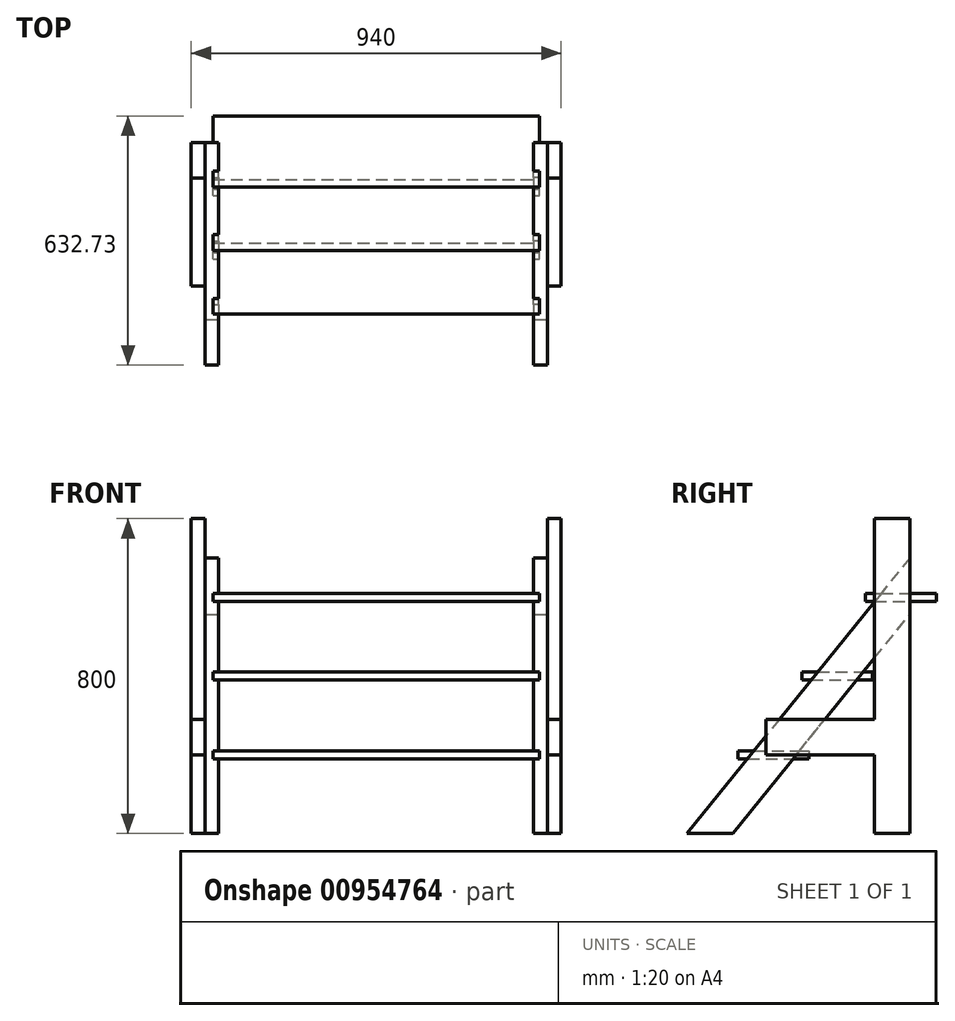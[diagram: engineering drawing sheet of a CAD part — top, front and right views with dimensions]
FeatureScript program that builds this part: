
annotation { "Feature Type Name" : "Feature", "Feature Type Description" : "" }
export const myFeature = defineFeature(function(context is Context, id is Id, definition is map)
    precondition{}
    {
        {
            var Q0;
            Q0=qCreatedBy(makeId("Right.planeOp"),FACE);
            var sketch = newSketch(context, id + "F0", { "sketchPlane" : qUnion([Q0])});
            skLineSegment(sketch, "E0.bottom", {"start": v(316.77, -269.2) * mm, "end": v(226.77, -269.2) * mm});
            skLineSegment(sketch, "E0.top", {"start": v(316.77, 530.8) * mm, "end": v(226.77, 530.8) * mm});
            skLineSegment(sketch, "E0.left", {"start": v(316.77, -269.2) * mm, "end": v(316.77, 530.8) * mm});
            skLineSegment(sketch, "E0.right", {"start": v(226.77, -269.2) * mm, "end": v(226.77, 530.8) * mm});
            skSolve(sketch);
        }
        {
            var Q0;
            Q0=makeQuery(id+"F0.imprint","IMPRINT",FACE,{"disambiguationData":[TD([[makeQuery(id+"F0.imprint","IMPRINT",EDGE,{"derivedFrom":sQuery(id+"F0.wireOp",EDGE,"E0.bottom")}),-1.0]])]});
            extrude(context, id + "F1", {"entities" : qUnion([Q0]), "depth" : 35 * mm, "offsetDistance" : 25 * mm});
        }
        {
            var Q0;
            Q0=makeQuery(id+"F1.opExtrude","CAP_FACE",FACE,{"disambiguationData":[OSD([sQuery(id+"F0.wireOp",EDGE,"E0.bottom"),sQuery(id+"F0.wireOp",EDGE,"E0.top"),sQuery(id+"F0.wireOp",EDGE,"E0.left"),sQuery(id+"F0.wireOp",EDGE,"E0.right")])],"isStart":true});
            var sketch = newSketch(context, id + "F2", { "sketchPlane" : qUnion([Q0])});
            skLineSegment(sketch, "E1", {"start": v(-316.77, 430.8) * mm, "end": v(248.91, -269.2) * mm});
            skLineSegment(sketch, "E2", {"start": v(-84.35, 0) * mm, "end": v(-316.77, 287.6) * mm});
            skLineSegment(sketch, "E3", {"start": v(-84.35, 0) * mm, "end": v(133.2, -269.2) * mm});
            skLineSegment(sketch, "E4", {"start": v(-316.77, 430.8) * mm, "end": v(-316.77, 287.6) * mm});
            skLineSegment(sketch, "E5", {"start": v(248.91, -269.2) * mm, "end": v(133.2, -269.2) * mm});
            skSolve(sketch);
        }
        {
            var Q0;
            Q0 = qSketchRegion(id + "F2", true);
            extrude(context, id + "F3", {"entities" : qUnion([Q0]), "operationType" : NewBodyOperationType.ADD, "depth" : 35 * mm, "offsetDistance" : 25 * mm});
        }
        {
            var Q0;
            Q0=makeQuery(id+"F1.opExtrude","SWEPT_FACE",FACE,{"disambiguationData":[OSD([sQuery(id+"F0.wireOp",EDGE,"E0.right")])]});
            var sketch = newSketch(context, id + "F4", { "sketchPlane" : qUnion([Q0])});
            skLineSegment(sketch, "E6", {"start": v(35, -69.2) * mm, "end": v(35, 23.34) * mm});
            skLineSegment(sketch, "E7.bottom", {"start": v(35, -69.2) * mm, "end": v(0, -69.2) * mm});
            skLineSegment(sketch, "E7.top", {"start": v(35, 20.8) * mm, "end": v(0, 20.8) * mm});
            skLineSegment(sketch, "E7.left", {"start": v(35, -69.2) * mm, "end": v(35, 20.8) * mm});
            skLineSegment(sketch, "E7.right", {"start": v(0, -69.2) * mm, "end": v(0, 20.8) * mm});
            skSolve(sketch);
        }
        {
            var Q0;
            Q0=makeQuery(id+"F3.opExtrude","CAP_FACE",FACE,{"disambiguationData":[OSD([sQuery(id+"F2.wireOp",EDGE,"E1"),sQuery(id+"F2.wireOp",EDGE,"E2"),sQuery(id+"F2.wireOp",EDGE,"E3"),sQuery(id+"F2.wireOp",EDGE,"E4"),sQuery(id+"F2.wireOp",EDGE,"E5")])],"isStart":false});
            var sketch = newSketch(context, id + "F5", { "sketchPlane" : qUnion([Q0])});
            skLineSegment(sketch, "E8.bottom", {"start": v(119.43, -59.2) * mm, "end": v(-60.57, -59.2) * mm});
            skLineSegment(sketch, "E8.top", {"start": v(119.43, -79.2) * mm, "end": v(-60.57, -79.2) * mm});
            skLineSegment(sketch, "E8.left", {"start": v(119.43, -59.2) * mm, "end": v(119.43, -79.2) * mm});
            skLineSegment(sketch, "E8.right", {"start": v(-60.57, -59.2) * mm, "end": v(-60.57, -79.2) * mm});
            skPoint(sketch, "E8.middle", {"position": v(29.43, -69.2) * mm});
            skLineSegment(sketch, "E9.bottom", {"start": v(-203.82, 340.8) * mm, "end": v(-383.82, 340.8) * mm});
            skLineSegment(sketch, "E9.top", {"start": v(-203.82, 320.8) * mm, "end": v(-383.82, 320.8) * mm});
            skLineSegment(sketch, "E9.left", {"start": v(-203.82, 340.8) * mm, "end": v(-203.82, 320.8) * mm});
            skLineSegment(sketch, "E9.right", {"start": v(-383.82, 340.8) * mm, "end": v(-383.82, 320.8) * mm});
            skPoint(sketch, "E9.middle", {"position": v(-293.82, 330.8) * mm});
            skLineSegment(sketch, "E10.bottom", {"start": v(-42.2, 140.8) * mm, "end": v(-222.2, 140.8) * mm});
            skLineSegment(sketch, "E10.top", {"start": v(-42.2, 120.8) * mm, "end": v(-222.2, 120.8) * mm});
            skLineSegment(sketch, "E10.left", {"start": v(-42.2, 140.8) * mm, "end": v(-42.2, 120.8) * mm});
            skLineSegment(sketch, "E10.right", {"start": v(-222.2, 140.8) * mm, "end": v(-222.2, 120.8) * mm});
            skPoint(sketch, "E10.middle", {"position": v(-132.2, 130.8) * mm});
            skSolve(sketch);
        }
        {
            var Q0;
            Q0 = qSketchRegion(id + "F5", true);
            extrude(context, id + "F6", {"entities" : qUnion([Q0]), "operationType" : NewBodyOperationType.ADD, "depth" : 800 * mm, "offsetDistance" : 25 * mm});
        }
        {
            var Q0;
            {var subQ0=sQuery(id+"F5.wireOp",EDGE,"E9.bottom");var subQ1=sQuery(id+"F2.wireOp",EDGE,"E4");var subQ2=sQuery(id+"F2.wireOp",EDGE,"E1");Q0=makeQuery(id+"F6.boolean.opBoolean","SPLIT",FACE,{"disambiguationData":[TD([makeQuery(id+"F6.opExtrude","SWEPT_FACE",FACE,{"disambiguationData":[OSD([subQ0])]})])],"derivedFrom":makeQuery(id+"F3.opExtrude","CAP_FACE",FACE,{"disambiguationData":[OSD([subQ2,sQuery(id+"F2.wireOp",EDGE,"E2"),sQuery(id+"F2.wireOp",EDGE,"E3"),subQ1,sQuery(id+"F2.wireOp",EDGE,"E5")])],"isStart":false})});}
            var sketch = newSketch(context, id + "F7", { "sketchPlane" : qUnion([Q0])});
            skLineSegment(sketch, "E11", {"start": v(-316.77, 430.8) * mm, "end": v(-316.77, 340.8) * mm});
            skLineSegment(sketch, "E12", {"start": v(-316.77, 340.8) * mm, "end": v(-244.04, 340.8) * mm});
            skLineSegment(sketch, "E13", {"start": v(-244.04, 340.8) * mm, "end": v(-316.77, 430.8) * mm});
            skSolve(sketch);
        }
        {
            var Q0;
            {var subQ0=sQuery(id+"F2.wireOp",EDGE,"E5");var subQ1=sQuery(id+"F2.wireOp",EDGE,"E4");var subQ2=sQuery(id+"F2.wireOp",EDGE,"E3");var subQ3=sQuery(id+"F2.wireOp",EDGE,"E2");var subQ4=sQuery(id+"F2.wireOp",EDGE,"E1");Q0=makeQuery(id+"FayiO8Eg1tZvXGc_1.boolean.opBoolean","MERGE",FACE,{"derivedFrom":[makeQuery(id+"F3Phc65WFf3S2oZ_1.boolean.opBoolean","MERGE",FACE,{"derivedFrom":[makeQuery(id+"F6.opExtrude","CAP_FACE",FACE,{"disambiguationData":[OSD([sQuery(id+"F5.wireOp",EDGE,"E8.bottom"),sQuery(id+"F5.wireOp",EDGE,"E8.top"),sQuery(id+"F5.wireOp",EDGE,"E8.left"),sQuery(id+"F5.wireOp",EDGE,"E8.right")])],"isStart":false}),makeQuery(id+"F3Phc65WFf3S2oZ_1.opExtrude","CAP_FACE",FACE,{"disambiguationData":[OSD([subQ4,subQ3,subQ2,subQ1,subQ0])],"isStart":false})]}),makeQuery(id+"FepYLJFoOySD3lM_1.boolean.opBoolean","MERGE",FACE,{"derivedFrom":[makeQuery(id+"F6.opExtrude","CAP_FACE",FACE,{"disambiguationData":[OSD([sQuery(id+"F5.wireOp",EDGE,"E10.bottom"),sQuery(id+"F5.wireOp",EDGE,"E10.top"),sQuery(id+"F5.wireOp",EDGE,"E10.left"),sQuery(id+"F5.wireOp",EDGE,"E10.right")])],"isStart":false}),makeQuery(id+"FOpsyVFvSxofQTJ_1.boolean.opBoolean","MERGE",FACE,{"derivedFrom":[makeQuery(id+"F6.opExtrude","CAP_FACE",FACE,{"disambiguationData":[OSD([sQuery(id+"F5.wireOp",EDGE,"E9.bottom"),sQuery(id+"F5.wireOp",EDGE,"E9.top"),sQuery(id+"F5.wireOp",EDGE,"E9.left"),sQuery(id+"F5.wireOp",EDGE,"E9.right")])],"isStart":false}),makeQuery(id+"FOpsyVFvSxofQTJ_1.opExtrude","CAP_FACE",FACE,{"disambiguationData":[OSD([sQuery(id+"F7.wireOp",EDGE,"E11"),sQuery(id+"F7.wireOp",EDGE,"E12"),sQuery(id+"F7.wireOp",EDGE,"E13")])],"isStart":false})]}),makeQuery(id+"FepYLJFoOySD3lM_1.opExtrude","CAP_FACE",FACE,{"disambiguationData":[OSD([subQ4,subQ3,subQ2,subQ1,subQ0])],"isStart":false})]}),makeQuery(id+"FayiO8Eg1tZvXGc_1.opExtrude","CAP_FACE",FACE,{"disambiguationData":[OSD([subQ4,subQ3,subQ2,subQ1,subQ0])],"isStart":false})]});}
            var sketch = newSketch(context, id + "F8", { "sketchPlane" : qUnion([Q0])});
            skLineSegment(sketch, "E14", {"start": v(-316.77, 287.6) * mm, "end": v(-316.77, 430.8) * mm});
            skLineSegment(sketch, "E15", {"start": v(-316.77, 430.8) * mm, "end": v(248.91, -269.2) * mm});
            skLineSegment(sketch, "E16", {"start": v(248.91, -269.2) * mm, "end": v(133.2, -269.2) * mm});
            skLineSegment(sketch, "E17", {"start": v(133.2, -269.2) * mm, "end": v(-316.77, 287.6) * mm});
            skSolve(sketch);
        }
        {
            var Q0;
            Q0 = qSketchRegion(id + "F8", true);
            extrude(context, id + "F9", {"entities" : qUnion([Q0]), "operationType" : NewBodyOperationType.ADD, "depth" : 35 * mm, "offsetDistance" : 25 * mm});
        }
        {
            var Q0;
            Q0=makeQuery(id+"F1PVaRCkqHldJCi_1.boolean.opBoolean","MERGE",FACE,{"derivedFrom":[makeQuery(id+"F9.opExtrude","CAP_FACE",FACE,{"disambiguationData":[OSD([sQuery(id+"F8.wireOp",EDGE,"E14"),sQuery(id+"F8.wireOp",EDGE,"E15"),sQuery(id+"F8.wireOp",EDGE,"E16"),sQuery(id+"F8.wireOp",EDGE,"E17")])],"isStart":false}),makeQuery(id+"F1PVaRCkqHldJCi_1.opExtrude","CAP_FACE",FACE,{"disambiguationData":[OSD([sQuery(id+"F0.wireOp",EDGE,"E0.top"),sQuery(id+"F0.wireOp",EDGE,"E0.left"),sQuery(id+"F0.wireOp",EDGE,"E0.right"),sQuery(id+"F2.wireOp",EDGE,"E1")])],"isStart":false})]});
            var sketch = newSketch(context, id + "F10", { "sketchPlane" : qUnion([Q0])});
            skPoint(sketch, "E18.oppositeSnap0", {"position": v(-226.77, 425.11) * mm});
            skLineSegment(sketch, "E18.bottom", {"start": v(-316.77, 530.8) * mm, "end": v(-226.77, 530.8) * mm});
            skLineSegment(sketch, "E18.top", {"start": v(-316.77, -269.2) * mm, "end": v(-226.77, -269.2) * mm});
            skLineSegment(sketch, "E18.left", {"start": v(-316.77, 530.8) * mm, "end": v(-316.77, -269.2) * mm});
            skLineSegment(sketch, "E18.right", {"start": v(-226.77, 530.8) * mm, "end": v(-226.77, -269.2) * mm});
            skSolve(sketch);
        }
        {
            var Q0;
            Q0 = qSketchRegion(id + "F10", true);
            extrude(context, id + "F11", {"entities" : qUnion([Q0]), "operationType" : NewBodyOperationType.ADD, "depth" : 35 * mm, "offsetDistance" : 25 * mm});
        }
        {
            var Q0;
            Q0=makeQuery(id+"F11.opExtrude","SWEPT_FACE",FACE,{"disambiguationData":[OSD([sQuery(id+"F10.wireOp",EDGE,"E18.right")])]});
            var sketch = newSketch(context, id + "F12", { "sketchPlane" : qUnion([Q0])});
            skLineSegment(sketch, "E19.bottom", {"start": v(-905, -69.2) * mm, "end": v(-870, -69.2) * mm});
            skLineSegment(sketch, "E19.top", {"start": v(-905, 20.8) * mm, "end": v(-870, 20.8) * mm});
            skLineSegment(sketch, "E19.left", {"start": v(-905, -69.2) * mm, "end": v(-905, 20.8) * mm});
            skLineSegment(sketch, "E19.right", {"start": v(-870, -69.2) * mm, "end": v(-870, 20.8) * mm});
            skSolve(sketch);
        }
        {
            var Q0;
            Q0 = qSketchRegion(id + "F12", true);
            extrude(context, id + "F13", {"entities" : qUnion([Q0]), "operationType" : NewBodyOperationType.ADD, "depth" : 275 * mm, "offsetDistance" : 25 * mm});
        }
        {
            var Q0;
            Q0 = qSketchRegion(id + "F4", true);
            extrude(context, id + "F14", {"entities" : qUnion([Q0]), "operationType" : NewBodyOperationType.ADD, "depth" : 275 * mm, "offsetDistance" : 25 * mm});
        }
        {
            var Q0;
            Q0 = qSketchRegion(id + "F5", true);
            extrude(context, id + "F15", {"entities" : qUnion([Q0]), "operationType" : NewBodyOperationType.ADD, "depth" : -15 * mm, "offsetDistance" : 25 * mm});
        }
        {
            var Q0;
            {var subQ1=sQuery(id+"F5.wireOp",EDGE,"E10.left");var subQ2=sQuery(id+"F5.wireOp",EDGE,"E10.top");var subQ3=sQuery(id+"F5.wireOp",EDGE,"E10.bottom");Q0=makeQuery(id+"F9.boolean.opBoolean","SPLIT",FACE,{"disambiguationData":[TD([makeQuery(id+"F6.opExtrude","SWEPT_FACE",FACE,{"disambiguationData":[OSD([subQ1])]})])],"derivedFrom":makeQuery(id+"F6.opExtrude","CAP_FACE",FACE,{"disambiguationData":[OSD([subQ3,subQ2,subQ1,sQuery(id+"F5.wireOp",EDGE,"E10.right")])],"isStart":false})});}
            extrude(context, id + "F16", {"entities" : qUnion([Q0]), "operationType" : NewBodyOperationType.ADD, "depth" : 15 * mm, "offsetDistance" : 25 * mm});
        }
        {
            var Q0;
            {var subQ1=sQuery(id+"F5.wireOp",EDGE,"E10.top");var subQ2=sQuery(id+"F5.wireOp",EDGE,"E10.right");var subQ3=sQuery(id+"F5.wireOp",EDGE,"E10.bottom");Q0=makeQuery(id+"F9.boolean.opBoolean","SPLIT",FACE,{"disambiguationData":[TD([makeQuery(id+"F6.opExtrude","SWEPT_FACE",FACE,{"disambiguationData":[OSD([subQ2])]})])],"derivedFrom":makeQuery(id+"F6.opExtrude","CAP_FACE",FACE,{"disambiguationData":[OSD([subQ3,subQ1,sQuery(id+"F5.wireOp",EDGE,"E10.left"),subQ2])],"isStart":false})});}
            extrude(context, id + "F17", {"entities" : qUnion([Q0]), "operationType" : NewBodyOperationType.ADD, "depth" : 15 * mm, "offsetDistance" : 25 * mm});
        }
        {
            var Q0;
            {var subQ0=sQuery(id+"F5.wireOp",EDGE,"E9.left");var subQ2=sQuery(id+"F5.wireOp",EDGE,"E9.top");var subQ3=sQuery(id+"F5.wireOp",EDGE,"E9.bottom");Q0=makeQuery(id+"F9.boolean.opBoolean","SPLIT",FACE,{"disambiguationData":[TD([makeQuery(id+"F6.opExtrude","SWEPT_FACE",FACE,{"disambiguationData":[OSD([subQ0])]})])],"derivedFrom":makeQuery(id+"F6.opExtrude","CAP_FACE",FACE,{"disambiguationData":[OSD([subQ3,subQ2,subQ0,sQuery(id+"F5.wireOp",EDGE,"E9.right")])],"isStart":false})});}
            extrude(context, id + "F18", {"entities" : qUnion([Q0]), "operationType" : NewBodyOperationType.ADD, "depth" : 15 * mm, "offsetDistance" : 25 * mm});
        }
        {
            var Q0;
            {var subQ1=sQuery(id+"F5.wireOp",EDGE,"E9.top");var subQ2=sQuery(id+"F5.wireOp",EDGE,"E9.right");var subQ3=sQuery(id+"F5.wireOp",EDGE,"E9.bottom");Q0=makeQuery(id+"F9.boolean.opBoolean","SPLIT",FACE,{"disambiguationData":[TD([makeQuery(id+"F6.opExtrude","SWEPT_FACE",FACE,{"disambiguationData":[OSD([subQ2])]})])],"derivedFrom":makeQuery(id+"F6.opExtrude","CAP_FACE",FACE,{"disambiguationData":[OSD([subQ3,subQ1,sQuery(id+"F5.wireOp",EDGE,"E9.left"),subQ2])],"isStart":false})});}
            extrude(context, id + "F19", {"entities" : qUnion([Q0]), "operationType" : NewBodyOperationType.ADD, "depth" : 15 * mm, "offsetDistance" : 25 * mm});
        }
        {
            var Q0;
            {var subQ1=sQuery(id+"F5.wireOp",EDGE,"E8.bottom");var subQ2=sQuery(id+"F5.wireOp",EDGE,"E8.left");var subQ3=sQuery(id+"F5.wireOp",EDGE,"E8.top");Q0=makeQuery(id+"F9.boolean.opBoolean","SPLIT",FACE,{"disambiguationData":[TD([makeQuery(id+"F6.opExtrude","SWEPT_FACE",FACE,{"disambiguationData":[OSD([subQ2])]})])],"derivedFrom":makeQuery(id+"F6.opExtrude","CAP_FACE",FACE,{"disambiguationData":[OSD([subQ1,subQ3,subQ2,sQuery(id+"F5.wireOp",EDGE,"E8.right")])],"isStart":false})});}
            var Q1;
            {var subQ1=sQuery(id+"F5.wireOp",EDGE,"E8.bottom");var subQ2=sQuery(id+"F5.wireOp",EDGE,"E8.top");var subQ3=sQuery(id+"F5.wireOp",EDGE,"E8.right");Q1=makeQuery(id+"F9.boolean.opBoolean","SPLIT",FACE,{"disambiguationData":[TD([makeQuery(id+"F6.opExtrude","SWEPT_FACE",FACE,{"disambiguationData":[OSD([subQ3])]})])],"derivedFrom":makeQuery(id+"F6.opExtrude","CAP_FACE",FACE,{"disambiguationData":[OSD([subQ1,subQ2,sQuery(id+"F5.wireOp",EDGE,"E8.left"),subQ3])],"isStart":false})});}
            extrude(context, id + "F20", {"entities" : qUnion([Q0, Q1]), "operationType" : NewBodyOperationType.ADD, "depth" : 15 * mm, "offsetDistance" : 25 * mm});
        }
    });
